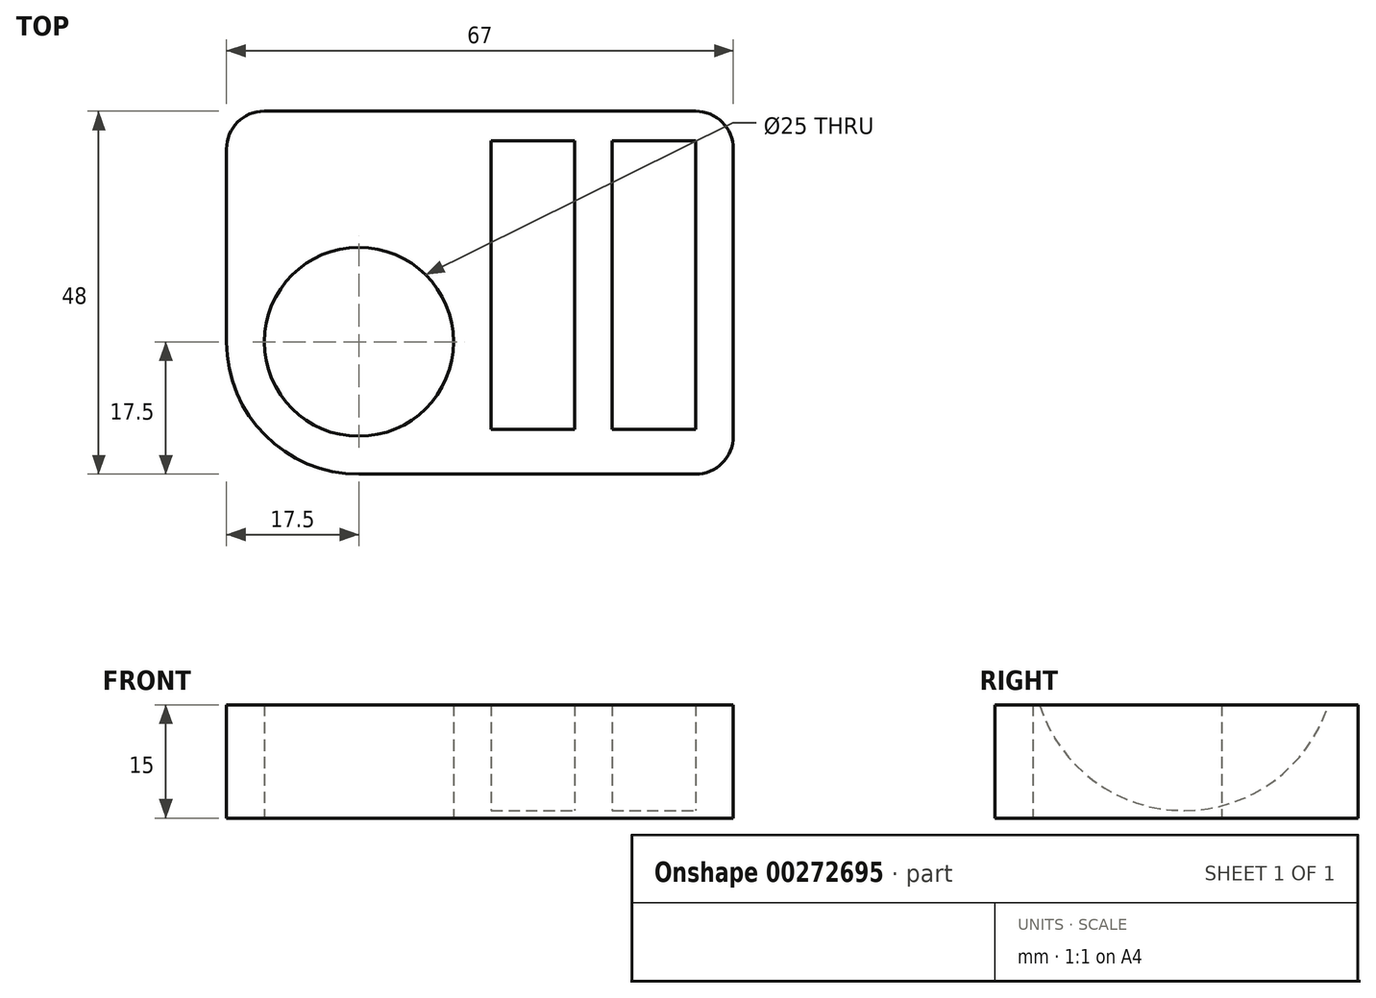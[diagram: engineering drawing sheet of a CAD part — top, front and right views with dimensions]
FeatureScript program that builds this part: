
annotation { "Feature Type Name" : "Feature", "Feature Type Description" : "" }
export const myFeature = defineFeature(function(context is Context, id is Id, definition is map)
    precondition{}
    {
        {
            var Q0;
            Q0=qCreatedBy(makeId("Top.planeOp"),FACE);
            var sketch = newSketch(context, id + "F0", { "sketchPlane" : qUnion([Q0])});
            skLineSegment(sketch, "E0.bottom", {"start": v(17.5, 0) * mm, "end": v(62, 0) * mm});
            skLineSegment(sketch, "E0.top", {"start": v(5, 48) * mm, "end": v(62, 48) * mm});
            skLineSegment(sketch, "E0.left", {"start": v(0, 17.5) * mm, "end": v(0, 43) * mm});
            skLineSegment(sketch, "E0.right", {"start": v(67, 5) * mm, "end": v(67, 43) * mm});
            skLineSegment(sketch, "E1.bottom", {"start": v(0, 0) * mm, "end": v(17.5, 0) * mm, "construction": true});
            skLineSegment(sketch, "E1.top", {"start": v(0, 17.5) * mm, "end": v(17.5, 17.5) * mm, "construction": true});
            skLineSegment(sketch, "E1.left", {"start": v(0, 0) * mm, "end": v(0, 17.5) * mm, "construction": true});
            skLineSegment(sketch, "E1.right", {"start": v(17.5, 0) * mm, "end": v(17.5, 17.5) * mm, "construction": true});
            skCircle(sketch, "E2", {"center": v(17.5, 17.5) * mm, "radius": 12.5 * mm});
            skPoint(sketch, "E3.visualSharp", {"position": v(0, 0) * mm});
            skArc(sketch, "E3.filletArc", {"start": v(0, 17.5) * mm, "mid": v(5.13, 5.13) * mm, "end": v(17.5, 0) * mm});
            skPoint(sketch, "E4.visualSharp", {"position": v(0, 48) * mm});
            skArc(sketch, "E4.filletArc", {"start": v(5, 48) * mm, "mid": v(1.46, 46.54) * mm, "end": v(0, 43) * mm});
            skPoint(sketch, "E5.visualSharp", {"position": v(67, 48) * mm});
            skArc(sketch, "E5.filletArc", {"start": v(67, 43) * mm, "mid": v(65.54, 46.54) * mm, "end": v(62, 48) * mm});
            skPoint(sketch, "E6.visualSharp", {"position": v(67, 0) * mm});
            skArc(sketch, "E6.filletArc", {"start": v(62, 0) * mm, "mid": v(65.54, 1.46) * mm, "end": v(67, 5) * mm});
            skSolve(sketch);
        }
        {
            var Q0;
            Q0=makeQuery(id+"F0.imprint","IMPRINT",FACE,{"disambiguationData":[TD([[makeQuery(id+"F0.imprint","IMPRINT",EDGE,{"derivedFrom":sQuery(id+"F0.wireOp",EDGE,"E0.bottom")}),1.0]])]});
            extrude(context, id + "F1", {"entities" : qUnion([Q0]), "depth" : 21 * mm});
        }
        {
            var Q0;
            Q0=makeQuery(id+"F1.opExtrude","CAP_FACE",FACE,{"disambiguationData":[OSD([sQuery(id+"F0.wireOp",EDGE,"E0.bottom"),sQuery(id+"F0.wireOp",EDGE,"E0.top"),sQuery(id+"F0.wireOp",EDGE,"E0.right"),sQuery(id+"F0.wireOp",EDGE,"E2"),sQuery(id+"F0.wireOp",EDGE,"E3.filletArc"),sQuery(id+"F0.wireOp",EDGE,"E4.filletArc"),sQuery(id+"F0.wireOp",EDGE,"E5.filletArc"),sQuery(id+"F0.wireOp",EDGE,"E6.filletArc")])],"isStart":false});
            var sketch = newSketch(context, id + "F2", { "sketchPlane" : qUnion([Q0])});
            skLineSegment(sketch, "E7.bottom", {"start": v(0, 0) * mm, "end": v(35, 0) * mm, "construction": true});
            skLineSegment(sketch, "E7.top", {"start": v(0, 25) * mm, "end": v(35, 25) * mm, "construction": true});
            skLineSegment(sketch, "E7.left", {"start": v(0, 0) * mm, "end": v(0, 25) * mm, "construction": true});
            skLineSegment(sketch, "E7.right", {"start": v(35, 0) * mm, "end": v(35, 25) * mm, "construction": true});
            skLineSegment(sketch, "E8.bottom", {"start": v(35, 25) * mm, "end": v(46, 25) * mm});
            skLineSegment(sketch, "E8.top", {"start": v(35, 5) * mm, "end": v(46, 5) * mm});
            skLineSegment(sketch, "E8.left", {"start": v(35, 25) * mm, "end": v(35, 5) * mm});
            skLineSegment(sketch, "E8.right", {"start": v(46, 25) * mm, "end": v(46, 5) * mm});
            skLineSegment(sketch, "E9", {"start": v(46, 25) * mm, "end": v(51, 25) * mm, "construction": true});
            skLineSegment(sketch, "E10.bottom", {"start": v(51, 25) * mm, "end": v(62, 25) * mm});
            skLineSegment(sketch, "E10.top", {"start": v(51, 5) * mm, "end": v(62, 5) * mm});
            skLineSegment(sketch, "E10.left", {"start": v(51, 25) * mm, "end": v(51, 5) * mm});
            skLineSegment(sketch, "E10.right", {"start": v(62, 25) * mm, "end": v(62, 5) * mm});
            skSolve(sketch);
        }
        {
            var Q0;
            Q0=makeQuery(id+"F2.imprint","IMPRINT",FACE,{"disambiguationData":[TD([[makeQuery(id+"F2.imprint","IMPRINT",EDGE,{"derivedFrom":sQuery(id+"F2.wireOp",EDGE,"E8.bottom")}),-1.0]])]});
            var Q1;
            Q1=makeQuery(id+"F2.imprint","IMPRINT",FACE,{"disambiguationData":[TD([[makeQuery(id+"F2.imprint","IMPRINT",EDGE,{"derivedFrom":sQuery(id+"F2.wireOp",EDGE,"E10.bottom")}),-1.0]])]});
            var Q2;
            Q2=sQuery(id+"F2.wireOp",EDGE,"E8.bottom");
            revolve(context, id + "F3", {"operationType" : NewBodyOperationType.REMOVE, "entities" : qUnion([Q0, Q1]), "axis" : qUnion([Q2]), "revolveType" : RevolveType.FULL, "oppositeDirection" : true});
        }
        {
            var Q0;
            Q0=makeQuery(id+"F1.opExtrude","SWEPT_FACE",FACE,{"disambiguationData":[OSD([sQuery(id+"F0.wireOp",EDGE,"E0.bottom")])]});
            var sketch = newSketch(context, id + "F4", { "sketchPlane" : qUnion([Q0])});
            skLineSegment(sketch, "E11", {"start": v(0, 0) * mm, "end": v(0, 15) * mm, "construction": true});
            skLineSegment(sketch, "E12.bottom", {"start": v(0, 15) * mm, "end": v(67.5, 15) * mm});
            skLineSegment(sketch, "E12.top", {"start": v(0, 21.78) * mm, "end": v(67.5, 21.78) * mm});
            skLineSegment(sketch, "E12.left", {"start": v(0, 15) * mm, "end": v(0, 21.78) * mm});
            skLineSegment(sketch, "E12.right", {"start": v(67.5, 15) * mm, "end": v(67.5, 21.78) * mm});
            skSolve(sketch);
        }
        {
            var Q0;
            Q0 = qSketchRegion(id + "F4", true);
            extrude(context, id + "F5", {"entities" : qUnion([Q0]), "operationType" : NewBodyOperationType.REMOVE, "endBound" : BoundingType.THROUGH_ALL, "oppositeDirection" : true, "depth" : 25 * mm});
        }
    });
